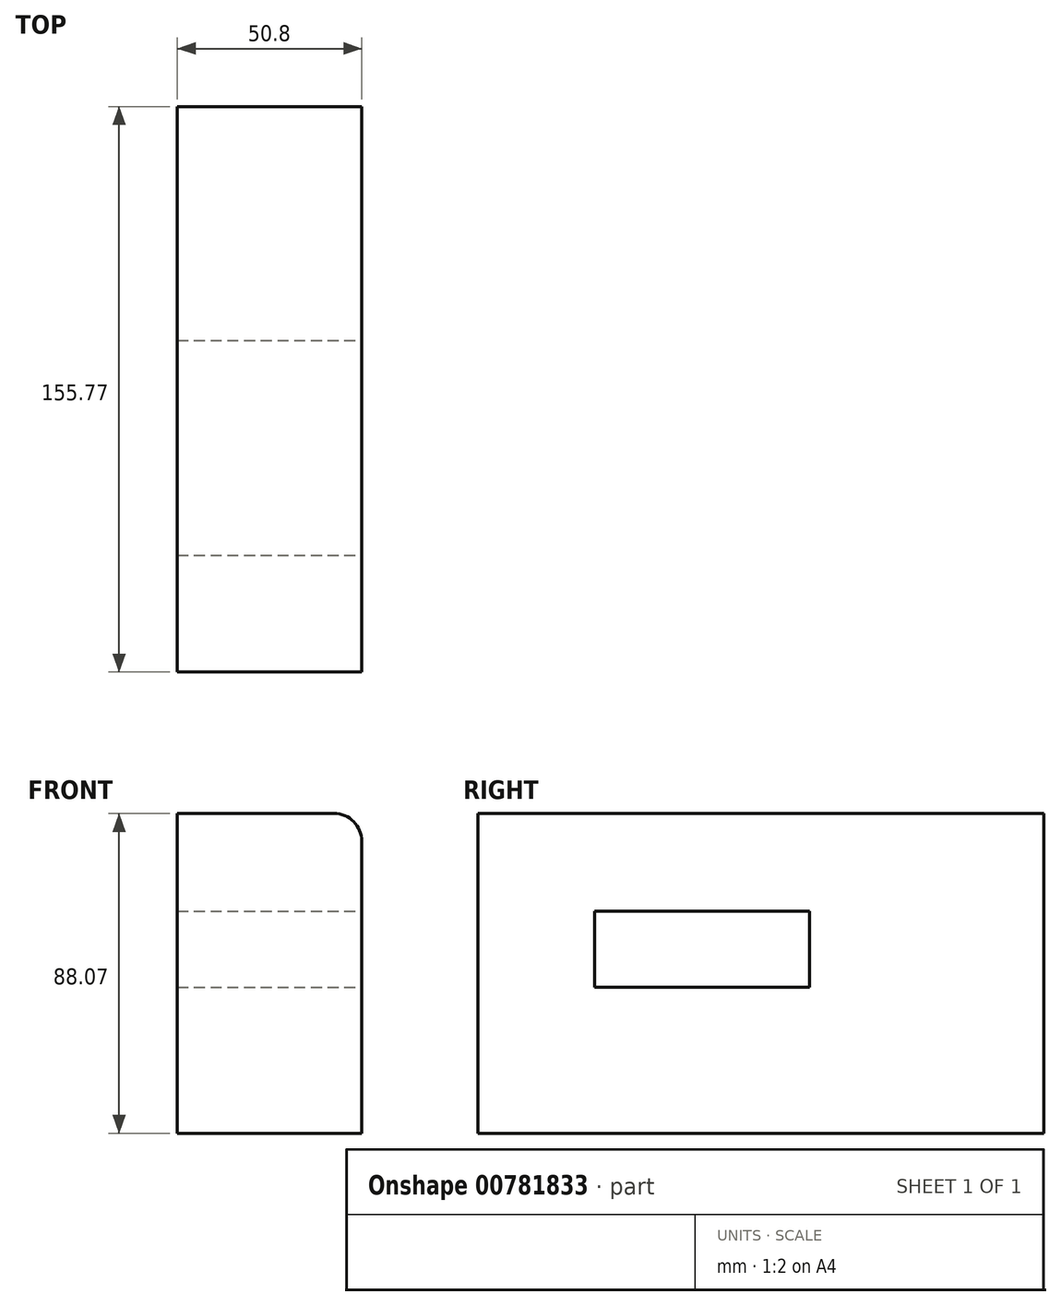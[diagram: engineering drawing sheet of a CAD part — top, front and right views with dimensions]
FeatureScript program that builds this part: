
annotation { "Feature Type Name" : "Feature", "Feature Type Description" : "" }
export const myFeature = defineFeature(function(context is Context, id is Id, definition is map)
    precondition{}
    {
        {
            var Q0;
            Q0=qCreatedBy(makeId("Right.planeOp"),FACE);
            var sketch = newSketch(context, id + "F0", { "sketchPlane" : qUnion([Q0])});
            skLineSegment(sketch, "E0.bottom", {"start": v(0, 0) * mm, "end": v(155.77, 0) * mm});
            skLineSegment(sketch, "E0.top", {"start": v(0, -88.07) * mm, "end": v(155.77, -88.07) * mm});
            skLineSegment(sketch, "E0.left", {"start": v(0, 0) * mm, "end": v(0, -88.07) * mm});
            skLineSegment(sketch, "E0.right", {"start": v(155.77, 0) * mm, "end": v(155.77, -88.07) * mm});
            skSolve(sketch);
        }
        {
            var Q0;
            Q0=makeQuery(id+"F0.imprint","IMPRINT",FACE,{"disambiguationData":[TD([[makeQuery(id+"F0.imprint","IMPRINT",EDGE,{"derivedFrom":sQuery(id+"F0.wireOp",EDGE,"E0.bottom")}),-1.0]])]});
            extrude(context, id + "F1", {"entities" : qUnion([Q0]), "depth" : 50.8 * mm, "offsetDistance" : 25.4 * mm});
        }
        {
            var Q0;
            Q0=makeQuery(id+"F1.opExtrude","CAP_EDGE",EDGE,{"disambiguationData":[OSD([sQuery(id+"F0.wireOp",EDGE,"E0.bottom")])],"isStart":false});
            fillet(context, id + "F2", {"entities" : qUnion([Q0]), "radius" : 7.62 * mm, "tangentPropagation" : true, "allowEdgeOverflow" : false});
        }
        {
            var Q0;
            Q0=makeQuery(id+"F1.opExtrude","CAP_FACE",FACE,{"disambiguationData":[OSD([sQuery(id+"F0.wireOp",EDGE,"E0.bottom"),sQuery(id+"F0.wireOp",EDGE,"E0.top"),sQuery(id+"F0.wireOp",EDGE,"E0.left"),sQuery(id+"F0.wireOp",EDGE,"E0.right")])],"isStart":false});
            var sketch = newSketch(context, id + "F3", { "sketchPlane" : qUnion([Q0])});
            skLineSegment(sketch, "E1.bottom", {"start": v(32.16, -47.85) * mm, "end": v(91.31, -47.85) * mm});
            skLineSegment(sketch, "E1.top", {"start": v(32.16, -26.95) * mm, "end": v(91.31, -26.95) * mm});
            skLineSegment(sketch, "E1.left", {"start": v(32.16, -47.85) * mm, "end": v(32.16, -26.95) * mm});
            skLineSegment(sketch, "E1.right", {"start": v(91.31, -47.85) * mm, "end": v(91.31, -26.95) * mm});
            skSolve(sketch);
        }
        {
            var Q0;
            Q0=makeQuery(id+"F3.imprint","IMPRINT",FACE,{"disambiguationData":[TD([[makeQuery(id+"F3.imprint","IMPRINT",EDGE,{"derivedFrom":sQuery(id+"F3.wireOp",EDGE,"E1.bottom")}),1.0]])]});
            extrude(context, id + "F4", {"entities" : qUnion([Q0]), "operationType" : NewBodyOperationType.REMOVE, "oppositeDirection" : true, "depth" : 50.8 * mm, "offsetDistance" : 25.4 * mm});
        }
    });
